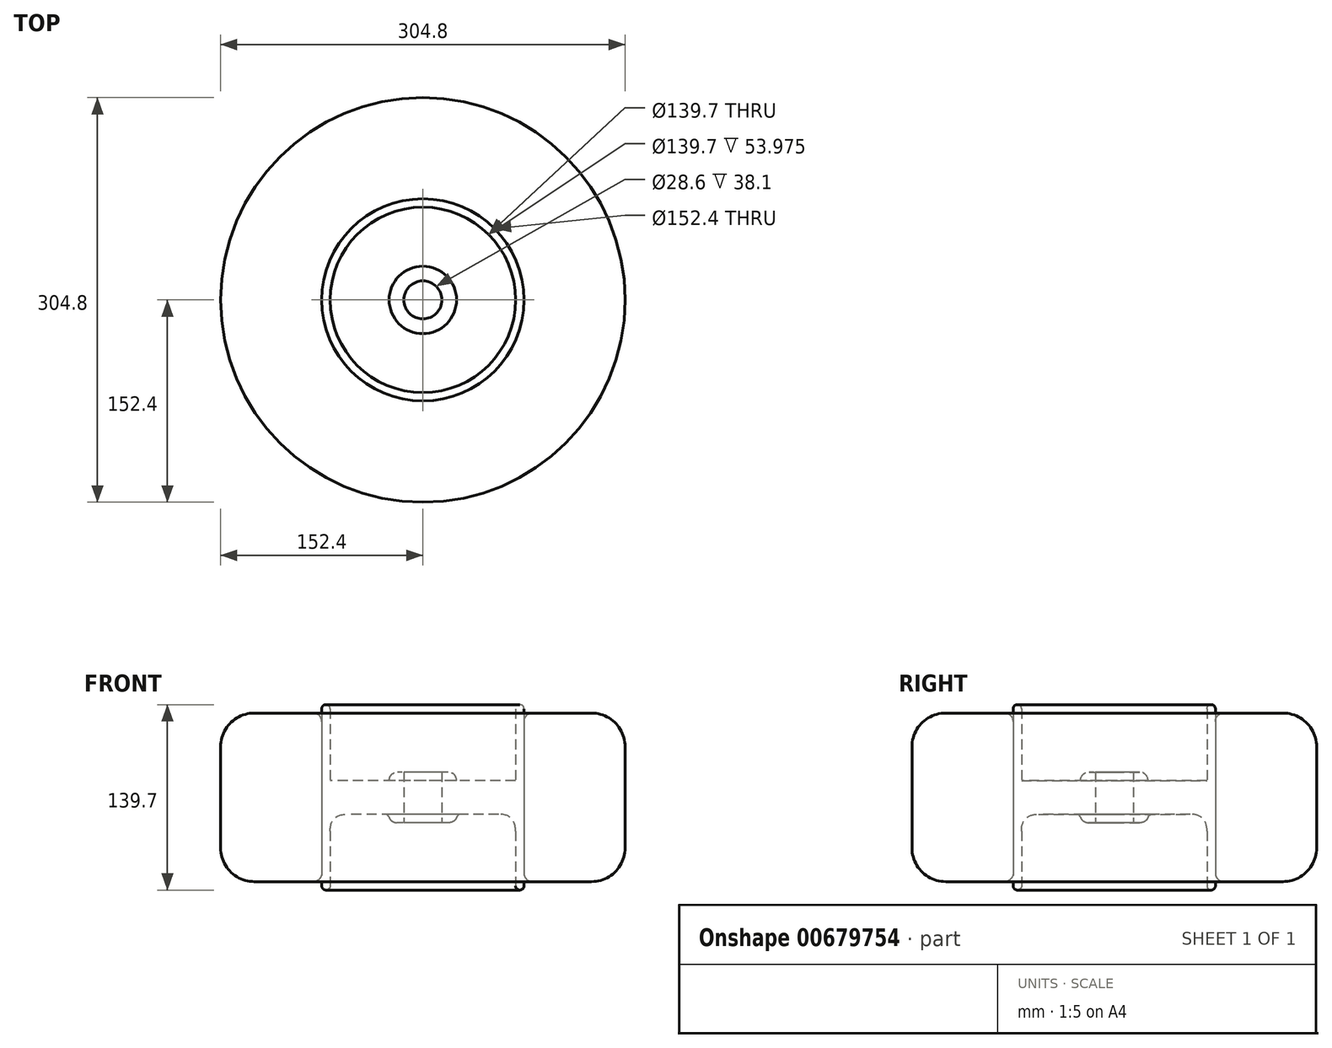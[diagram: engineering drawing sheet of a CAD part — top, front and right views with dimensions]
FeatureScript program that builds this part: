
annotation { "Feature Type Name" : "Feature", "Feature Type Description" : "" }
export const myFeature = defineFeature(function(context is Context, id is Id, definition is map)
    precondition{}
    {
        {
            var Q0;
            Q0=qCreatedBy(makeId("Top.planeOp"),FACE);
            var sketch = newSketch(context, id + "F0", { "sketchPlane" : qUnion([Q0])});
            skCircle(sketch, "E0", {"center": v(0, 0) * mm, "radius": 152.4 * mm});
            skCircle(sketch, "E1", {"center": v(0, 0) * mm, "radius": 76.2 * mm});
            skSolve(sketch);
        }
        {
            var Q0;
            Q0=makeQuery(id+"F0.imprint","IMPRINT",FACE,{"disambiguationData":[TD([[makeQuery(id+"F0.imprint","IMPRINT",EDGE,{"derivedFrom":sQuery(id+"F0.wireOp",EDGE,"E0")}),1.0]])]});
            extrude(context, id + "F1", {"entities" : qUnion([Q0]), "endBound" : BoundingType.SYMMETRIC, "depth" : 127 * mm, "offsetDistance" : 25.4 * mm});
        }
        {
            var Q0;
            Q0=qCreatedBy(makeId("Top.planeOp"),FACE);
            var sketch = newSketch(context, id + "F2", { "sketchPlane" : qUnion([Q0])});
            skCircle(sketch, "E2", {"center": v(0, 0) * mm, "radius": 76.2 * mm});
            skCircle(sketch, "E3", {"center": v(0, 0) * mm, "radius": 69.85 * mm});
            skSolve(sketch);
        }
        {
            var Q0;
            Q0=makeQuery(id+"F2.imprint","IMPRINT",FACE,{"disambiguationData":[TD([[makeQuery(id+"F2.imprint","IMPRINT",EDGE,{"derivedFrom":sQuery(id+"F2.wireOp",EDGE,"E2")}),1.0]])]});
            extrude(context, id + "F3", {"entities" : qUnion([Q0]), "endBound" : BoundingType.SYMMETRIC, "depth" : 139.7 * mm, "offsetDistance" : 25.4 * mm});
        }
        {
            var Q0;
            Q0=qCreatedBy(makeId("Top.planeOp"),FACE);
            var sketch = newSketch(context, id + "F4", { "sketchPlane" : qUnion([Q0])});
            skCircle(sketch, "E4", {"center": v(0, 0) * mm, "radius": 69.85 * mm});
            skCircle(sketch, "E5", {"center": v(0, 0) * mm, "radius": 25.4 * mm});
            skSolve(sketch);
        }
        {
            var Q0;
            Q0=makeQuery(id+"F4.imprint","IMPRINT",FACE,{"disambiguationData":[TD([[makeQuery(id+"F4.imprint","IMPRINT",EDGE,{"derivedFrom":sQuery(id+"F4.wireOp",EDGE,"E4")}),1.0]])]});
            extrude(context, id + "F5", {"entities" : qUnion([Q0]), "operationType" : NewBodyOperationType.ADD, "endBound" : BoundingType.SYMMETRIC, "depth" : 25.4 * mm, "offsetDistance" : 25.4 * mm});
        }
        {
            var Q0;
            Q0=qCreatedBy(makeId("Top.planeOp"),FACE);
            var sketch = newSketch(context, id + "F6", { "sketchPlane" : qUnion([Q0])});
            skCircle(sketch, "E6", {"center": v(0, 0) * mm, "radius": 14.3 * mm});
            skCircle(sketch, "E7", {"center": v(0, 0) * mm, "radius": 25.4 * mm});
            skSolve(sketch);
        }
        {
            var Q0;
            Q0=makeQuery(id+"F6.imprint","IMPRINT",FACE,{"disambiguationData":[TD([[makeQuery(id+"F6.imprint","IMPRINT",EDGE,{"derivedFrom":sQuery(id+"F6.wireOp",EDGE,"E6")}),-1.0]])]});
            extrude(context, id + "F7", {"entities" : qUnion([Q0]), "operationType" : NewBodyOperationType.ADD, "endBound" : BoundingType.SYMMETRIC, "depth" : 38.1 * mm, "offsetDistance" : 25.4 * mm});
        }
        {
            var Q0;
            Q0=makeQuery(id+"F1.opExtrude","CAP_EDGE",EDGE,{"disambiguationData":[OSD([sQuery(id+"F0.wireOp",EDGE,"E1")])],"isStart":false});
            var Q1;
            Q1=makeQuery(id+"F1.opExtrude","CAP_EDGE",EDGE,{"disambiguationData":[OSD([sQuery(id+"F0.wireOp",EDGE,"E1")])],"isStart":true});
            fillet(context, id + "F8", {"entities" : qUnion([Q0, Q1]), "radius" : 6.35 * mm, "tangentPropagation" : true, "allowEdgeOverflow" : false});
        }
        {
            var Q0;
            Q0=makeQuery(id+"F1.opExtrude","SWEPT_FACE",FACE,{"disambiguationData":[OSD([sQuery(id+"F0.wireOp",EDGE,"E0")])]});
            fillet(context, id + "F9", {"entities" : qUnion([Q0]), "radius" : 25.4 * mm, "tangentPropagation" : true, "allowEdgeOverflow" : false});
        }
        {
            var Q0;
            Q0=makeQuery(id+"F3.opExtrude","CAP_FACE",FACE,{"disambiguationData":[OSD([sQuery(id+"F2.wireOp",EDGE,"E2"),sQuery(id+"F2.wireOp",EDGE,"E3")])],"isStart":true});
            var Q1;
            Q1=makeQuery(id+"F3.opExtrude","CAP_FACE",FACE,{"disambiguationData":[OSD([sQuery(id+"F2.wireOp",EDGE,"E2"),sQuery(id+"F2.wireOp",EDGE,"E3")])],"isStart":false});
            fillet(context, id + "F10", {"entities" : qUnion([Q0, Q1]), "radius" : 3.17 * mm, "tangentPropagation" : true, "allowEdgeOverflow" : false});
        }
        {
            var Q0;
            Q0=makeQuery(id+"F5.opExtrude","CAP_EDGE",EDGE,{"disambiguationData":[OSD([sQuery(id+"F4.wireOp",EDGE,"E4")])],"isStart":true});
            var Q1;
            Q1=makeQuery(id+"F5.opExtrude","CAP_EDGE",EDGE,{"disambiguationData":[OSD([sQuery(id+"F4.wireOp",EDGE,"E4")])],"isStart":false});
            fillet(context, id + "F11", {"entities" : qUnion([Q0, Q1]), "radius" : 12.7 * mm, "tangentPropagation" : true, "rho" : 0.5, "crossSection" : FilletCrossSection.CONIC, "allowEdgeOverflow" : false});
        }
        {
            var Q0;
            Q0=makeQuery(id+"F5.opExtrude","CAP_EDGE",EDGE,{"disambiguationData":[OSD([sQuery(id+"F4.wireOp",EDGE,"E5")])],"isStart":false});
            var Q1;
            Q1=makeQuery(id+"F5.opExtrude","CAP_EDGE",EDGE,{"disambiguationData":[OSD([sQuery(id+"F4.wireOp",EDGE,"E5")])],"isStart":true});
            fillet(context, id + "F12", {"entities" : qUnion([Q0, Q1]), "radius" : 3.17 * mm, "tangentPropagation" : true, "allowEdgeOverflow" : false});
        }
        {
            var Q0;
            Q0=makeQuery(id+"F7.opExtrude","CAP_EDGE",EDGE,{"disambiguationData":[OSD([sQuery(id+"F6.wireOp",EDGE,"E7")])],"isStart":true});
            var Q1;
            Q1=makeQuery(id+"F7.opExtrude","CAP_EDGE",EDGE,{"disambiguationData":[OSD([sQuery(id+"F6.wireOp",EDGE,"E7")])],"isStart":false});
            fillet(context, id + "F13", {"entities" : qUnion([Q0, Q1]), "radius" : 6.35 * mm, "tangentPropagation" : true, "allowEdgeOverflow" : false});
        }
    });
